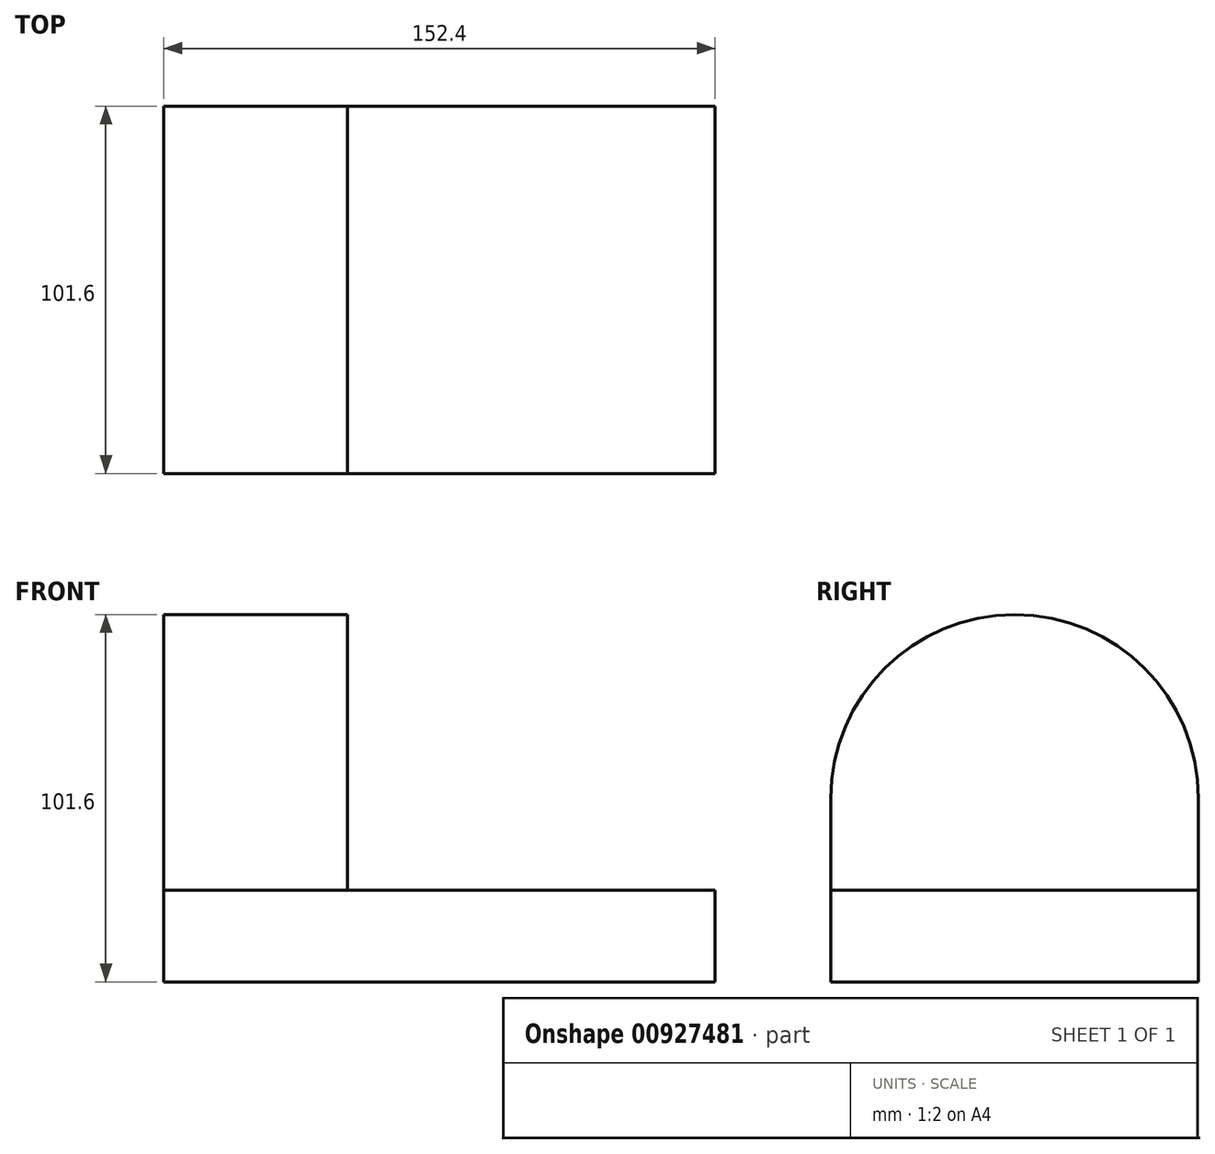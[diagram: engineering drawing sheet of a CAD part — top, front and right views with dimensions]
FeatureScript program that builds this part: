
annotation { "Feature Type Name" : "Feature", "Feature Type Description" : "" }
export const myFeature = defineFeature(function(context is Context, id is Id, definition is map)
    precondition{}
    {
        {
            var Q0;
            Q0=qCreatedBy(makeId("Right.planeOp"),FACE);
            var sketch = newSketch(context, id + "F0", { "sketchPlane" : qUnion([Q0])});
            skLineSegment(sketch, "E0.bottom", {"start": v(0, 0) * mm, "end": v(101.6, 0) * mm});
            skLineSegment(sketch, "E0.top", {"start": v(0, 25.4) * mm, "end": v(101.6, 25.4) * mm});
            skLineSegment(sketch, "E0.left", {"start": v(0, 0) * mm, "end": v(0, 25.4) * mm});
            skLineSegment(sketch, "E0.right", {"start": v(101.6, 0) * mm, "end": v(101.6, 25.4) * mm});
            skSolve(sketch);
        }
        {
            var Q0;
            Q0 = qSketchRegion(id + "F0", true);
            extrude(context, id + "F1", {"entities" : qUnion([Q0]), "depth" : 152.4 * mm, "offsetDistance" : 25.4 * mm});
        }
        {
            var Q0;
            Q0=makeQuery(id+"F1.opExtrude","CAP_FACE",FACE,{"disambiguationData":[OSD([sQuery(id+"F0.wireOp",EDGE,"E0.bottom"),sQuery(id+"F0.wireOp",EDGE,"E0.top"),sQuery(id+"F0.wireOp",EDGE,"E0.left"),sQuery(id+"F0.wireOp",EDGE,"E0.right")])],"isStart":true});
            var sketch = newSketch(context, id + "F2", { "sketchPlane" : qUnion([Q0])});
            skArc(sketch, "E1", {"start": v(0, 50.8) * mm, "mid": v(-50.8, 101.6) * mm, "end": v(-101.6, 50.8) * mm});
            skLineSegment(sketch, "E2", {"start": v(0, 50.8) * mm, "end": v(0, 25.4) * mm});
            skLineSegment(sketch, "E3", {"start": v(-101.6, 50.8) * mm, "end": v(-101.6, 25.4) * mm});
            skSolve(sketch);
        }
        {
            var Q0;
            Q0=makeQuery(id+"F2.imprint","IMPRINT",FACE,{"disambiguationData":[TD([[makeQuery(id+"F2.imprint","IMPRINT",EDGE,{"derivedFrom":sQuery(id+"F2.wireOp",EDGE,"E1")}),1.0]])]});
            extrude(context, id + "F3", {"entities" : qUnion([Q0]), "oppositeDirection" : true, "depth" : 50.8 * mm, "offsetDistance" : 25.4 * mm});
        }
    });
